# Revit family: BA-08
name_source: partatom
category: Устройства связи
revit_build: Autodesk Revit 2016 (Build: 20160314_0715(x64)
units: mm (PartAtom-declared; Revit-internal decimal feet)

## family parameters
Всегда вертикально = Нет
На основе рабочей плоскости = Да
Общий = Да
При загрузке вырезать с полостями = Нет
Размер круглого соединителя = Использовать диаметр
Сохранять ориентацию аннотаций = Нет
Тип детали = Нормальный
Точка расчета площади = Нет

## types (1)
- BA-08
    ADSK_URL документации изделия = https://wiki.bas-ip.com
    ADSK_URL страницы изделия = https://www.bas-ip.ru
    ADSK_Версия Revit = Revit 2016
    ADSK_Единица измерения = шт
    ADSK_Завод-изготовитель = BAS-IP
    ADSK_Классификация нагрузок = Вызывная панель
    ADSK_Количество фаз = 1
    ADSK_Коэффициент мощности = 0.9
    ADSK_Марка = BA-08
    ADSK_Наименование = ВЫЗЫВНАЯ ПАНЕЛЬ BA-08
    ADSK_Наименование краткое = BA-08
    ADSK_Напряжение = 12 В
    ADSK_Номинальная мощность = 7 Вт
    ADSK_Полная мощность = 7 В·А
    ADSK_Размер_Длина = 155 мм
    ADSK_Размер_Толщина = 50 мм
    ADSK_Размер_Ширина = 270 мм
    BIM library = https://bimlib.ru
    URL = https://www.bas-ip.ru
    Аутентификация = Отдельный пароль на настройки, WEB–интерфейс
    Выходное видео = D1 (704х576), H.264 Main Profile, BaseLine Profile
    Группа модели = Вызывная панель
    Дисплей = Нет
    Дополнительно = SIP P2P, Встроенное реле
    Изготовитель = BAS-IP
    Изображение = SHV_Изображение_BA-08
    Изображение типоразмера = <Нет>
    Интеграция со СКУД = Выход WIEGAND-26
    Интерфейс = WEB-интерфейс
    Камера = 1/3”, регулировка направления камеры
    Класс степени защиты = IP65
    Кнопки быстрого вызова = Кнопка вызова консьержа
    Количество мелодий вызова = 4 полифонические мелодии
    Контроль доступа = Считыватель беcконтактных карт EM-Marin (BA-04E), Mifare (BA-04M)
    Корпус = Металлический
    Материал корпуса = Серебро
    Минимальная освещенность = 0,01 LuX
    Ночная подсветка = 6 светодиодов
    Описание = Многоабонентская вызывная панель BA-08 – это прекрасный выбор для тех, кто задумался об установке вызывной панели в небольшом офисном центре до 8 офисов, многоквартирном доме, таунхаусе или же дуплексе.
    Открытие замка = С монитора, по карте, из приложения BAS-IP Intercom
    Отметка по умолчанию = 0 мм
    Питание = +12 В
    Потребление питания = 6,5 Вт, в режиме ожидания – 2,5 Вт
    Размер под установку = 150х250х60 мм
    Размер самой панели = 155х270х50 мм
    Разрешение камеры = 800 ТВл
    Режим разговора = Двухсторонний
    Температурный режим = -40 ... +65 °С
    Тип клавиатуры = Механические кнопки с подсветкой
    Тип панели = Многоквартирная
    Тип установки = Врезная, накладная с BR-BA
    Угол обзора = По горизонтали 78°, по вертикали 56°
    Цветовое решение = Серебристо-серый
